# Revit family: Window_Curtain_Wall-Project_Out-Kawneer-AA4325
name_source: partatom
category: Windows
revit_build: Autodesk Revit 2015 (Build: 20140905_0730(x64)
units: mm (PartAtom-declared; Revit-internal decimal feet)

## types (1)
- AA4325 - Project_Out - Vent
    Assembly Code = B2020110
    CTRL Center Mullion L/R Offset = 0' - 1 1/8"
    CTRL Center Mullion Visibility = No
    CTRL Center Mullion Visibility 2 = Yes
    CTRL Center Mullion Width = 0' - 1 1/4"
    CTRL Configuration Number = 1
    CTRL Fixed Panel Top Visibility = No
    CTRL Fixed Panel Top Visibility 2 = No
    CTRL Mullion Fixed Visibility = No
    CTRL Panel Active Frame Width = 0' - 2 3/8"
    CTRL Panel Middle Visibility 2 = No
    CTRL Top Mullion Offset = 0' - 1 1/8"
    Depth = 0' - 3 1/4"
    Description = Project Out Window
    Fixed Jamb Width = 0' - 2 1/4"
    Fixed Sill Width = 0' - 2 1/4"
    Frame Material = Metal - Kawneer - Aluminum
    Glazing Material = Glass - Kawneer - Clear
    Has Fixed Panel Bottom = No
    Has Fixed Panel Top = No
    Head Width = 0' - 3 3/8"
    Height Maximum = 3' - 0"
    Height Minimum = 1' - 7"
    Jamb Width = 0' - 3 3/8"
    Manufacturer = Kawneer
    Model = AA 4325
    Panel Configuration = Vent
    Product data url = https://bimobject.com
    Sill Width = 0' - 3 3/8"
    URL = http://www.kawneer.com
    Width Maximum = 5' - 0"
    Width Minimum = 2' - 0"

## geometry (parser evidence)
native form markers: Blend x4, Sweep x2
no freeform markers — native parametric forms only
